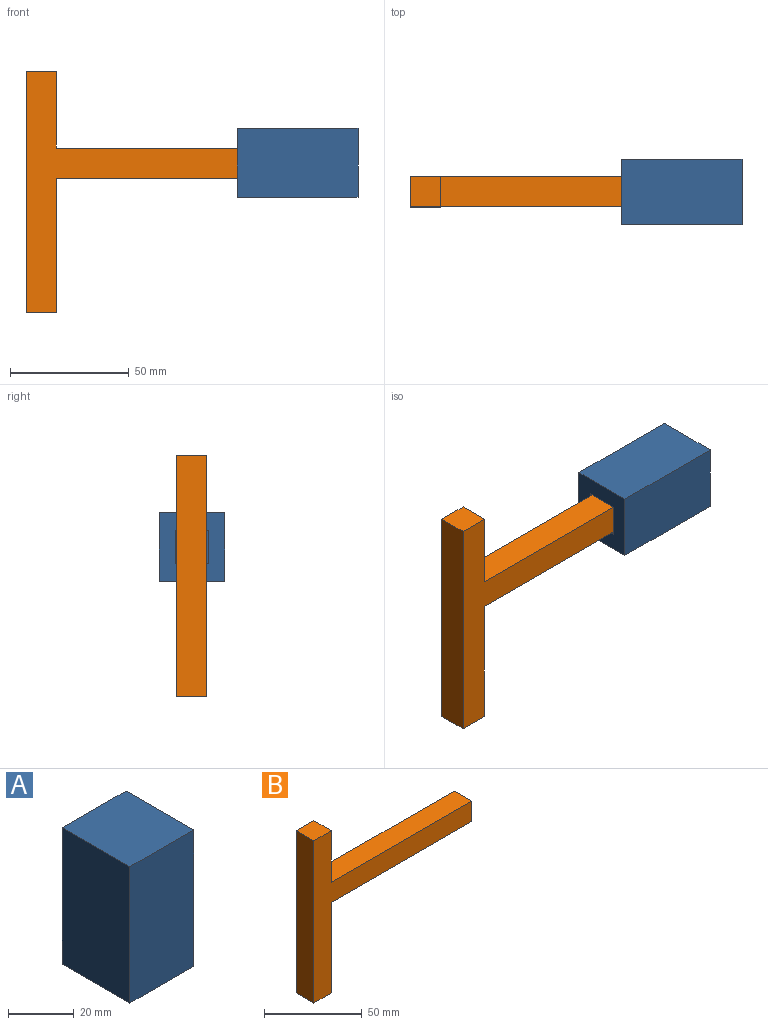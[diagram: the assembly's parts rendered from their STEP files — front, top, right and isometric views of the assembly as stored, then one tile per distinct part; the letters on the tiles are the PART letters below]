
ASSEMBLY  parts=2 mates=1
PART A: 11 faces, bbox 27.4x29x50.8 mm
  f0: plane 25.4x13.97mm, normal (1,0,0), area 354.8mm2, adj f1,f3,f9,f10
  f1: plane 25.4x13.97mm, normal (0,-1,0), area 354.8mm2, adj f0,f2,f9,f10
  f2: plane 25.4x13.97mm, normal (-1,0,0), area 354.8mm2, adj f1,f3,f9,f10
  f3: plane 25.4x13.97mm, normal (0,1,0), area 354.8mm2, adj f0,f2,f9,f10
  f4: plane 50.8x27.36mm, normal (0,1,0), area 1389.9mm2, adj f5,f7,f8,f9
  f5: plane 50.8x29.02mm, normal (-1,0,0), area 1474.2mm2, adj f4,f6,f8,f9
  f6: plane 50.8x27.36mm, normal (0,-1,0), area 1389.9mm2, adj f5,f7,f8,f9
  f7: plane 50.8x29.02mm, normal (1,0,0), area 1474.2mm2, adj f4,f6,f8,f9
  f8: plane 29.02x27.36mm, normal (0,0,1), area 794mm2, adj f4,f5,f6,f7
  f9: plane 29.02x27.36mm, normal (0,0,-1), area 598.8mm2, adj f0,f1,f2,f3,f4,f5,f6,f7
  f10: plane 13.97x13.97mm, normal (0,0,-1), area 195.2mm2, adj f0,f1,f2,f3
PART B: 10 faces, bbox 114.3x12.7x101.6 mm
  f0: plane 12.7x12.7mm, normal (0,0,1), area 161.3mm2, adj f1,f7,f8,f9
  f1: plane 101.6x12.7mm, normal (-1,0,0), area 1290.3mm2, adj f0,f2,f8,f9
  f2: plane 12.7x12.7mm, normal (0,0,-1), area 161.3mm2, adj f1,f3,f8,f9
  f3: plane 56.6x12.7mm, normal (1,0,0), area 718.9mm2, adj f2,f4,f8,f9
  f4: plane 101.6x12.7mm, normal (0,0,-1), area 1290.3mm2, adj f3,f5,f8,f9
  f5: plane 12.7x12.7mm, normal (1,0,0), area 161.3mm2, adj f4,f6,f8,f9
  f6: plane 101.6x12.7mm, normal (0,0,1), area 1290.3mm2, adj f5,f7,f8,f9
  f7: plane 32.3x12.7mm, normal (1,0,0), area 410.2mm2, adj f0,f6,f8,f9
  f8: plane 114.3x101.6mm, normal (0,-1,0), area 2580.6mm2, adj f0,f1,f2,f3,f4,f5,f6,f7
  f9: plane 114.3x101.6mm, normal (0,1,0), area 2580.6mm2, adj f0,f1,f2,f3,f4,f5,f6,f7
PLACE A rot(axis=(0.58,0.58,0.58),120deg) t=(35.85,8.79,-0.2)mm
PLACE B t=(-36.23,-16.85,9.32)mm
MATE fastened A.f10 <-> B.f5  axis (-1,0,0) through (35.85,-16.85,35.25)mm
